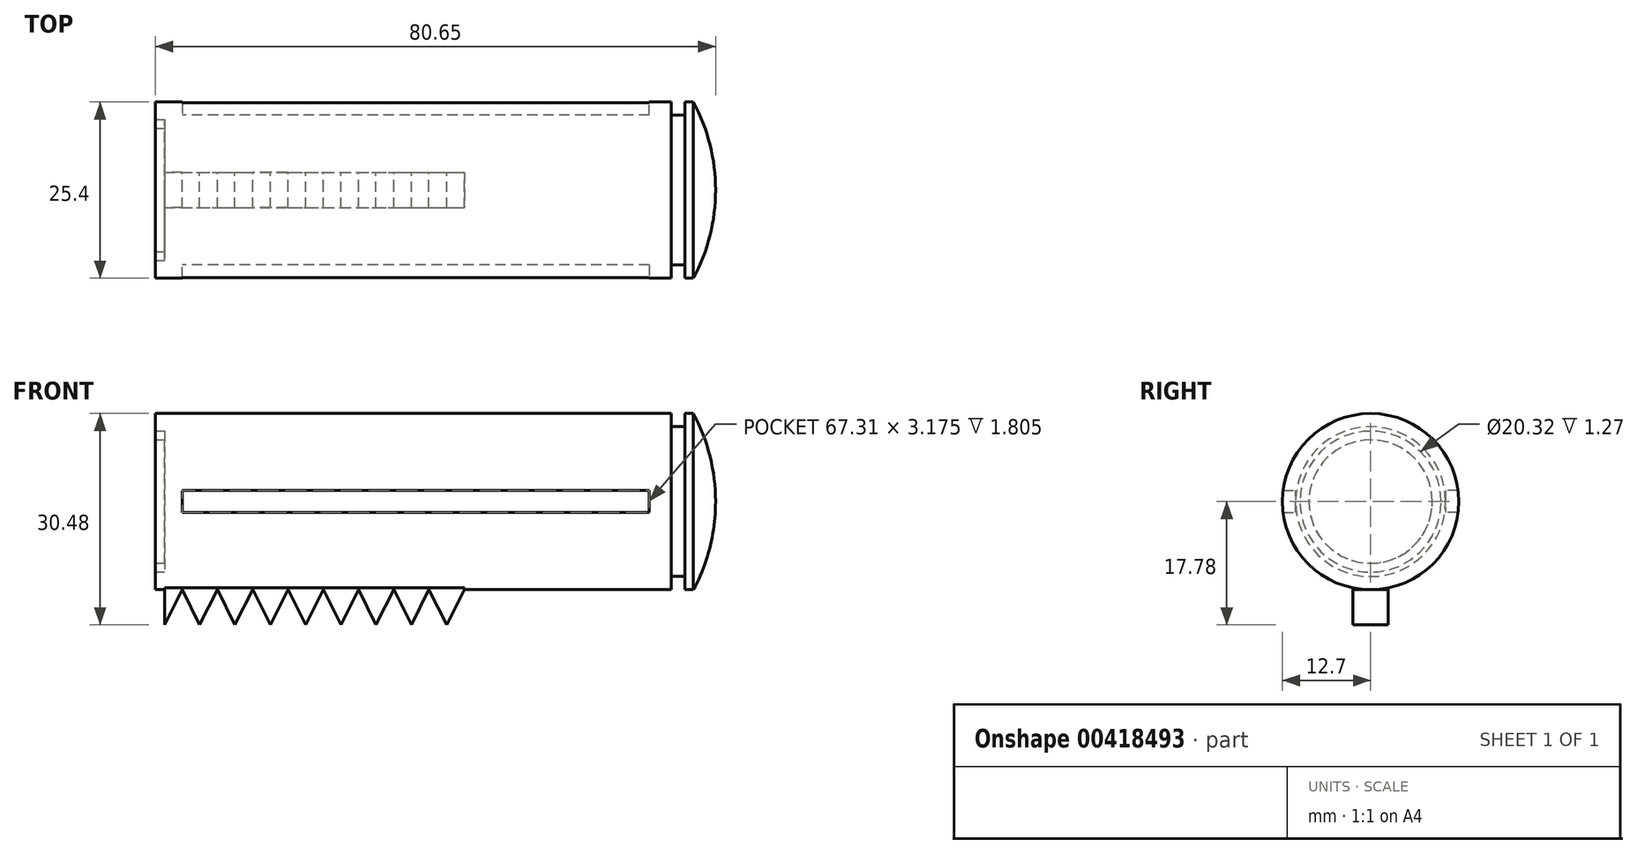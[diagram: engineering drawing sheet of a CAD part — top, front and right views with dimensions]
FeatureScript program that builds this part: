
annotation { "Feature Type Name" : "Feature", "Feature Type Description" : "" }
export const myFeature = defineFeature(function(context is Context, id is Id, definition is map)
    precondition{}
    {
        {
            var Q0;
            Q0=qCreatedBy(makeId("Front.planeOp"),FACE);
            var sketch = newSketch(context, id + "F0", { "sketchPlane" : qUnion([Q0])});
            skLineSegment(sketch, "E0", {"start": v(0, 0) * mm, "end": v(-76.2, 0) * mm});
            skLineSegment(sketch, "E1", {"start": v(-76.2, 0) * mm, "end": v(-76.2, -12.7) * mm});
            skLineSegment(sketch, "E2", {"start": v(-76.2, -12.7) * mm, "end": v(-3.17, -12.7) * mm});
            skLineSegment(sketch, "E3", {"start": v(0, -12.7) * mm, "end": v(0, 0) * mm});
            skLineSegment(sketch, "E4", {"start": v(0, 0) * mm, "end": v(3.18, 0) * mm});
            skArc(sketch, "E5", {"start": v(0, -12.7) * mm, "mid": v(2.37, -6.55) * mm, "end": v(3.17, 0) * mm});
            skPoint(sketch, "E6.end.orphan", {"position": v(0, 12.7) * mm});
            skLineSegment(sketch, "E7", {"start": v(-3.18, -10.8) * mm, "end": v(-3.18, -12.7) * mm});
            skLineSegment(sketch, "E8", {"start": v(-3.18, -10.8) * mm, "end": v(-1.27, -10.8) * mm});
            skLineSegment(sketch, "E9", {"start": v(-1.27, -10.8) * mm, "end": v(-1.27, -12.7) * mm});
            skLineSegment(sketch, "E10", {"start": v(-1.27, -12.7) * mm, "end": v(0, -12.7) * mm});
            skSolve(sketch);
        }
        {
            var Q0;
            Q0=makeQuery(id+"F0.imprint","IMPRINT",FACE,{"disambiguationData":[TD([[makeQuery(id+"F0.imprint","IMPRINT",EDGE,{"derivedFrom":sQuery(id+"F0.wireOp",EDGE,"E0")}),1.0]])]});
            var Q1;
            Q1=makeQuery(id+"F0.imprint","IMPRINT",FACE,{"disambiguationData":[TD([[makeQuery(id+"F0.imprint","IMPRINT",EDGE,{"derivedFrom":sQuery(id+"F0.wireOp",EDGE,"E3")}),-1.0]])]});
            var Q2;
            Q2=sQuery(id+"F0.wireOp",EDGE,"E0");
            revolve(context, id + "F1", {"entities" : qUnion([Q0, Q1]), "axis" : qUnion([Q2]), "revolveType" : RevolveType.FULL});
        }
        {
            var Q0;
            Q0=qCreatedBy(makeId("Front.planeOp"),FACE);
            var sketch = newSketch(context, id + "F2", { "sketchPlane" : qUnion([Q0])});
            skPoint(sketch, "E11", {"position": v(-73.66, -12.7) * mm});
            skPoint(sketch, "E12", {"position": v(-68.58, -12.7) * mm});
            skPoint(sketch, "E13", {"position": v(-63.5, -12.7) * mm});
            skPoint(sketch, "E14", {"position": v(-58.42, -12.7) * mm});
            skPoint(sketch, "E15", {"position": v(-53.34, -12.7) * mm});
            skPoint(sketch, "E16", {"position": v(-48.26, -12.7) * mm});
            skPoint(sketch, "E17", {"position": v(-43.18, -12.7) * mm});
            skPoint(sketch, "E18", {"position": v(-38.1, -12.7) * mm});
            skPoint(sketch, "E19", {"position": v(-33.02, -12.7) * mm});
            skLineSegment(sketch, "E20", {"start": v(-76.2, -12.7) * mm, "end": v(-76.2, -17.78) * mm});
            skLineSegment(sketch, "E21", {"start": v(-73.66, -12.7) * mm, "end": v(-76.2, -17.78) * mm});
            skPoint(sketch, "E22", {"position": v(-71.12, -17.78) * mm});
            skPoint(sketch, "E23", {"position": v(-66.04, -17.78) * mm});
            skPoint(sketch, "E24", {"position": v(-60.96, -17.78) * mm});
            skPoint(sketch, "E25", {"position": v(-55.88, -17.78) * mm});
            skPoint(sketch, "E26", {"position": v(-50.8, -17.78) * mm});
            skPoint(sketch, "E27", {"position": v(-45.72, -17.78) * mm});
            skPoint(sketch, "E28", {"position": v(-40.64, -17.78) * mm});
            skPoint(sketch, "E29", {"position": v(-35.56, -17.78) * mm});
            skLineSegment(sketch, "E30", {"start": v(-73.66, -12.7) * mm, "end": v(-71.12, -17.78) * mm});
            skLineSegment(sketch, "E31", {"start": v(-71.12, -17.78) * mm, "end": v(-68.58, -12.7) * mm});
            skLineSegment(sketch, "E32", {"start": v(-68.58, -12.7) * mm, "end": v(-66.04, -17.78) * mm});
            skLineSegment(sketch, "E33", {"start": v(-66.04, -17.78) * mm, "end": v(-63.5, -12.7) * mm});
            skLineSegment(sketch, "E34", {"start": v(-58.42, -12.7) * mm, "end": v(-60.96, -17.78) * mm});
            skLineSegment(sketch, "E35", {"start": v(-58.42, -12.7) * mm, "end": v(-55.88, -17.78) * mm});
            skLineSegment(sketch, "E36", {"start": v(-55.88, -17.78) * mm, "end": v(-53.34, -12.7) * mm});
            skLineSegment(sketch, "E37", {"start": v(-53.34, -12.7) * mm, "end": v(-50.8, -17.78) * mm});
            skLineSegment(sketch, "E38", {"start": v(-50.8, -17.78) * mm, "end": v(-48.26, -12.7) * mm});
            skLineSegment(sketch, "E39", {"start": v(-48.26, -12.7) * mm, "end": v(-45.72, -17.78) * mm});
            skLineSegment(sketch, "E40", {"start": v(-45.72, -17.78) * mm, "end": v(-43.18, -12.7) * mm});
            skLineSegment(sketch, "E41", {"start": v(-43.18, -12.7) * mm, "end": v(-40.64, -17.78) * mm});
            skLineSegment(sketch, "E42", {"start": v(-40.64, -17.78) * mm, "end": v(-38.1, -12.7) * mm});
            skLineSegment(sketch, "E43", {"start": v(-38.1, -12.7) * mm, "end": v(-35.56, -17.78) * mm});
            skLineSegment(sketch, "E44", {"start": v(-35.56, -17.78) * mm, "end": v(-33.02, -12.7) * mm});
            skLineSegment(sketch, "E45", {"start": v(-33.02, -10.16) * mm, "end": v(-76.2, -10.16) * mm});
            skLineSegment(sketch, "E46", {"start": v(-33.02, -12.7) * mm, "end": v(-33.02, -10.16) * mm});
            skPoint(sketch, "E47.orphan", {"position": v(0, -10.16) * mm});
            skPoint(sketch, "E48.orphan", {"position": v(0, -12.7) * mm});
            skPoint(sketch, "E49.trimOffspring.end.orphan", {"position": v(0, -17.78) * mm});
            skLineSegment(sketch, "E50", {"start": v(-60.96, -17.78) * mm, "end": v(-63.5, -12.7) * mm});
            skLineSegment(sketch, "E51", {"start": v(-76.2, -12.7) * mm, "end": v(-76.2, -10.16) * mm});
            skSolve(sketch);
        }
        {
            var Q0;
            {var subQ0=sQuery(id+"F2.wireOp",EDGE,"E20");Q0=makeQuery(id+"F2.imprint","IMPRINT",FACE,{"disambiguationData":[TD([[makeQuery(id+"F2.imprint","IMPRINT",EDGE,{"derivedFrom":subQ0}),1.0]])]});}
            var Q1;
            {var subQ0=sQuery(id+"F2.wireOp",EDGE,"E30");Q1=makeQuery(id+"F2.imprint","IMPRINT",FACE,{"disambiguationData":[TD([[makeQuery(id+"F2.imprint","IMPRINT",EDGE,{"derivedFrom":subQ0}),1.0]])]});}
            var Q2;
            {var subQ0=sQuery(id+"F2.wireOp",EDGE,"E35");Q2=makeQuery(id+"F2.imprint","IMPRINT",FACE,{"disambiguationData":[TD([[makeQuery(id+"F2.imprint","IMPRINT",EDGE,{"derivedFrom":subQ0}),1.0]])]});}
            var Q3;
            {var subQ0=sQuery(id+"F2.wireOp",EDGE,"E32");Q3=makeQuery(id+"F2.imprint","IMPRINT",FACE,{"disambiguationData":[TD([[makeQuery(id+"F2.imprint","IMPRINT",EDGE,{"derivedFrom":subQ0}),1.0]])]});}
            var Q4;
            {var subQ0=sQuery(id+"F2.wireOp",EDGE,"E37");Q4=makeQuery(id+"F2.imprint","IMPRINT",FACE,{"disambiguationData":[TD([[makeQuery(id+"F2.imprint","IMPRINT",EDGE,{"derivedFrom":subQ0}),1.0]])]});}
            var Q5;
            {var subQ0=sQuery(id+"F2.wireOp",EDGE,"E39");Q5=makeQuery(id+"F2.imprint","IMPRINT",FACE,{"disambiguationData":[TD([[makeQuery(id+"F2.imprint","IMPRINT",EDGE,{"derivedFrom":subQ0}),1.0]])]});}
            var Q6;
            {var subQ0=sQuery(id+"F2.wireOp",EDGE,"E41");Q6=makeQuery(id+"F2.imprint","IMPRINT",FACE,{"disambiguationData":[TD([[makeQuery(id+"F2.imprint","IMPRINT",EDGE,{"derivedFrom":subQ0}),1.0]])]});}
            extrude(context, id + "F3", {"entities" : qUnion([Q0, Q1, Q2, Q3, Q4, Q5, Q6]), "operationType" : NewBodyOperationType.ADD, "endBound" : BoundingType.SYMMETRIC, "depth" : 5.08 * mm});
        }
        {
            var Q0;
            Q0=makeQuery(id+"F3.boolean.opBoolean","MERGE",FACE,{"derivedFrom":[makeQuery(id+"F1.opRevolve","SWEPT_FACE",FACE,{"disambiguationData":[OSD([sQuery(id+"F0.wireOp",EDGE,"E1")])]}),makeQuery(id+"F3.opExtrude","SWEPT_FACE",FACE,{"disambiguationData":[OSD([sQuery(id+"F2.wireOp",EDGE,"E20"),sQuery(id+"F2.wireOp",EDGE,"E51")])]})]});
            var sketch = newSketch(context, id + "F4", { "sketchPlane" : qUnion([Q0])});
            skLineSegment(sketch, "E52", {"start": v(12.7, 0) * mm, "end": v(12.7, -1.59) * mm});
            skLineSegment(sketch, "E53", {"start": v(10.8, 0) * mm, "end": v(10.8, -1.59) * mm});
            skLineSegment(sketch, "E54", {"start": v(10.8, -1.59) * mm, "end": v(12.7, -1.59) * mm});
            skLineSegment(sketch, "E55.MirrorCS", {"start": v(10.8, 0) * mm, "end": v(10.8, 1.59) * mm});
            skLineSegment(sketch, "E56.MirrorCS", {"start": v(10.8, 1.59) * mm, "end": v(12.7, 1.59) * mm});
            skLineSegment(sketch, "E57.MirrorCS", {"start": v(12.7, 0) * mm, "end": v(12.7, 1.59) * mm});
            skLineSegment(sketch, "E58.MirrorCS", {"start": v(-10.8, 0) * mm, "end": v(-10.8, 1.59) * mm});
            skLineSegment(sketch, "E59.MirrorCS", {"start": v(-10.8, 1.59) * mm, "end": v(-12.7, 1.59) * mm});
            skLineSegment(sketch, "E60.MirrorCS", {"start": v(-12.7, 0) * mm, "end": v(-12.7, -1.59) * mm});
            skLineSegment(sketch, "E61.MirrorCS", {"start": v(-12.7, 0) * mm, "end": v(-12.7, 1.59) * mm});
            skLineSegment(sketch, "E62.MirrorCS", {"start": v(-10.8, 0) * mm, "end": v(-10.8, -1.59) * mm});
            skLineSegment(sketch, "E63.MirrorCS", {"start": v(-10.8, -1.59) * mm, "end": v(-12.7, -1.59) * mm});
            skSolve(sketch);
        }
        {
            var Q0;
            {var subQ2=sQuery(id+"F4.wireOp",EDGE,"E58.MirrorCS");Q0=makeQuery(id+"F4.imprint","IMPRINT",FACE,{"disambiguationData":[TD([[makeQuery(id+"F4.imprint","IMPRINT",EDGE,{"derivedFrom":subQ2}),1.0]])]});}
            var Q1;
            {var subQ5=sQuery(id+"F4.wireOp",EDGE,"E53");Q1=makeQuery(id+"F4.imprint","IMPRINT",FACE,{"disambiguationData":[TD([[makeQuery(id+"F4.imprint","IMPRINT",EDGE,{"derivedFrom":subQ5}),1.0]])]});}
            extrude(context, id + "F5", {"entities" : qUnion([Q0, Q1]), "operationType" : NewBodyOperationType.REMOVE, "oppositeDirection" : true, "depth" : 69.85 * mm});
        }
        {
            var Q0;
            Q0=makeQuery(id+"F3.boolean.opBoolean","MERGE",FACE,{"derivedFrom":[makeQuery(id+"F1.opRevolve","SWEPT_FACE",FACE,{"disambiguationData":[OSD([sQuery(id+"F0.wireOp",EDGE,"E1")])]}),makeQuery(id+"F3.opExtrude","SWEPT_FACE",FACE,{"disambiguationData":[OSD([sQuery(id+"F2.wireOp",EDGE,"E20"),sQuery(id+"F2.wireOp",EDGE,"E51")])]})]});
            var sketch = newSketch(context, id + "F6", { "sketchPlane" : qUnion([Q0])});
            skCircle(sketch, "E64", {"center": v(0, 0) * mm, "radius": 12.7 * mm});
            skSolve(sketch);
        }
        {
            var Q0;
            Q0 = qSketchRegion(id + "F6", true);
            extrude(context, id + "F7", {"entities" : qUnion([Q0]), "operationType" : NewBodyOperationType.ADD, "depth" : -2.54 * mm});
        }
        {
            var Q0;
            Q0=makeQuery(id+"F7.boolean.opBoolean","MERGE",FACE,{"derivedFrom":[makeQuery(id+"F3.boolean.opBoolean","MERGE",FACE,{"derivedFrom":[makeQuery(id+"F1.opRevolve","SWEPT_FACE",FACE,{"disambiguationData":[OSD([sQuery(id+"F0.wireOp",EDGE,"E1")])]}),makeQuery(id+"F3.opExtrude","SWEPT_FACE",FACE,{"disambiguationData":[OSD([sQuery(id+"F2.wireOp",EDGE,"E20"),sQuery(id+"F2.wireOp",EDGE,"E51")])]})]}),makeQuery(id+"F7.opExtrude","CAP_FACE",FACE,{"disambiguationData":[OSD([sQuery(id+"F6.wireOp",EDGE,"E64")])],"isStart":true})]});
            var sketch = newSketch(context, id + "F8", { "sketchPlane" : qUnion([Q0])});
            skCircle(sketch, "E65", {"center": v(0, 0) * mm, "radius": 12.7 * mm});
            skCircle(sketch, "E66", {"center": v(0, 0) * mm, "radius": 10.16 * mm});
            skCircle(sketch, "E67", {"center": v(0, 0) * mm, "radius": 8.9 * mm});
            skSolve(sketch);
        }
        {
            var Q0;
            {var subQ0=sQuery(id+"F8.wireOp",EDGE,"E65");Q0=makeQuery(id+"F8.imprint","IMPRINT",FACE,{"disambiguationData":[TD([[makeQuery(id+"F8.imprint","IMPRINT",EDGE,{"disambiguationData":[OD(0.0)],"derivedFrom":subQ0}),-1.0]])]});}
            extrude(context, id + "F9", {"entities" : qUnion([Q0]), "operationType" : NewBodyOperationType.ADD, "depth" : 1.27 * mm});
        }
        {
            var Q0;
            Q0=makeQuery(id+"F8.imprint","IMPRINT",FACE,{"disambiguationData":[TD([[makeQuery(id+"F8.imprint","IMPRINT",EDGE,{"derivedFrom":sQuery(id+"F8.wireOp",EDGE,"E67")}),1.0]])]});
            extrude(context, id + "F10", {"entities" : qUnion([Q0]), "operationType" : NewBodyOperationType.ADD, "depth" : 1.27 * mm});
        }
    });
